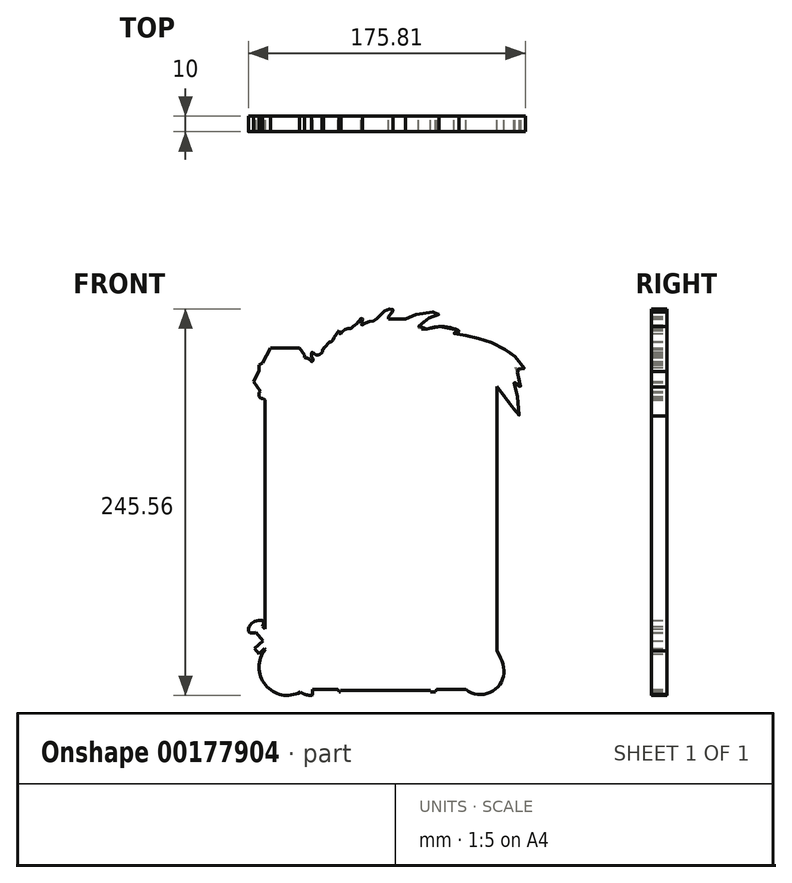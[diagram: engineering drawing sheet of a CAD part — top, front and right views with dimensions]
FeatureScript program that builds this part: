
annotation { "Feature Type Name" : "Feature", "Feature Type Description" : "" }
export const myFeature = defineFeature(function(context is Context, id is Id, definition is map)
    precondition{}
    {
        {
            var Q0;
            Q0=qCreatedBy(makeId("Front.planeOp"),FACE);
            var sketch = newSketch(context, id + "F0", { "sketchPlane" : qUnion([Q0])});
            skLineSegment(sketch, "E0", {"start": v(-74.75, 64.26) * mm, "end": v(-74.75, -81.01) * mm});
            skLineSegment(sketch, "E1", {"start": v(-74.75, -81.01) * mm, "end": v(-76.46, -79.38) * mm});
            skFitSpline(sketch, "E2", {"points": [v(-76.46, -79.38) * mm, v(-75.9, -76.2) * mm, v(-82.58, -77.01) * mm, v(-85.03, -82.89) * mm, v(-80.38, -83.46) * mm], "startDerivative": vector(9.15, 18.87) * mm, "endDerivative": vector(25.07, 3.1) * mm});
            skLineSegment(sketch, "E3", {"start": v(-80.38, -83.46) * mm, "end": v(-76, -88.76) * mm});
            skLineSegment(sketch, "E4", {"start": v(-76, -88.76) * mm, "end": v(-81.56, -93.36) * mm});
            skLineSegment(sketch, "E5", {"start": v(-81.56, -93.36) * mm, "end": v(-78.6, -96.95) * mm});
            skLineSegment(sketch, "E6", {"start": v(-78.6, -96.95) * mm, "end": v(-75.2, -93.38) * mm});
            skLineSegment(sketch, "E7", {"start": v(-75.2, -93.38) * mm, "end": v(-74.52, -94.03) * mm});
            skArc(sketch, "E8", {"start": v(-74.52, -94.03) * mm, "mid": v(-74.52, -116.71) * mm, "end": v(-52.3, -121.24) * mm});
            skLineSegment(sketch, "E9", {"start": v(-44.65, -119.52) * mm, "end": v(-28.42, -119.52) * mm});
            skLineSegment(sketch, "E10", {"start": v(-28.42, -119.52) * mm, "end": v(-28.42, -120.3) * mm});
            skLineSegment(sketch, "E11", {"start": v(-28.42, -120.3) * mm, "end": v(-27.65, -120.3) * mm});
            skLineSegment(sketch, "E12", {"start": v(-27.65, -120.3) * mm, "end": v(-27.65, -121) * mm});
            skLineSegment(sketch, "E13", {"start": v(-27.65, -121) * mm, "end": v(-26.8, -121) * mm});
            skLineSegment(sketch, "E14", {"start": v(-26.8, -121) * mm, "end": v(-26.8, -120.3) * mm});
            skLineSegment(sketch, "E15", {"start": v(-26.8, -120.3) * mm, "end": v(30.46, -120.3) * mm});
            skLineSegment(sketch, "E16", {"start": v(30.46, -120.3) * mm, "end": v(30.46, -121) * mm});
            skLineSegment(sketch, "E17", {"start": v(30.46, -121) * mm, "end": v(33.58, -121) * mm});
            skLineSegment(sketch, "E18", {"start": v(33.58, -121) * mm, "end": v(33.58, -120.3) * mm});
            skLineSegment(sketch, "E19", {"start": v(33.58, -120.3) * mm, "end": v(34.25, -120.3) * mm});
            skLineSegment(sketch, "E20", {"start": v(34.25, -120.3) * mm, "end": v(34.25, -119.52) * mm});
            skLineSegment(sketch, "E21", {"start": v(34.25, -119.52) * mm, "end": v(53.01, -119.52) * mm});
            skFitSpline(sketch, "E22", {"points": [v(53.01, -119.52) * mm, v(67.33, -121.84) * mm, v(76.63, -111.23) * mm, v(72.63, -95.04) * mm], "startDerivative": vector(33.7, -30.73) * mm, "endDerivative": vector(-27.31, 51.01) * mm});
            skLineSegment(sketch, "E23", {"start": v(72.63, -95.04) * mm, "end": v(72.63, 72.94) * mm});
            skFitSpline(sketch, "E24", {"points": [v(72.63, 72.94) * mm, v(85.97, 54.17) * mm, v(85.54, 65.97) * mm, v(83.67, 75.34) * mm, v(87.15, 72.72) * mm, v(86.43, 79.92) * mm, v(84.26, 85.01) * mm, v(90.27, 82.4) * mm, v(86.43, 89.5) * mm, v(80.55, 94.68) * mm, v(70.51, 100.26) * mm, v(61.21, 103.39) * mm, v(52.27, 105.35) * mm, v(45.25, 106.45) * mm, v(48.35, 107.87) * mm, v(37.59, 110.97) * mm, v(27.39, 109.45) * mm, v(22.83, 110.32) * mm, v(27.4, 115.4) * mm, v(34.53, 117.92) * mm, v(35.8, 119.1) * mm, v(33.75, 120.16) * mm, v(19.92, 118.15) * mm, v(14.36, 115.66) * mm], "startDerivative": vector(228.47, -153.01) * mm, "endDerivative": vector(-97.64, -55.3) * mm});
            skLineSegment(sketch, "E25", {"start": v(14.36, 115.66) * mm, "end": v(3.54, 115.66) * mm});
            skLineSegment(sketch, "E26", {"start": v(3.54, 115.66) * mm, "end": v(3.54, 117.49) * mm});
            skFitSpline(sketch, "E27", {"points": [v(3.54, 117.49) * mm, v(6.45, 121.85) * mm, v(1.12, 120.69) * mm, v(-4.7, 115.06) * mm, v(-9.7, 113.76) * mm, v(-13.63, 112.06) * mm, v(-13.7, 113.48) * mm, v(-12.87, 114.86) * mm, v(-13.04, 116.42) * mm, v(-15.65, 113.86) * mm, v(-17.1, 111.96) * mm, v(-18.36, 111.62) * mm, v(-19.71, 110.02) * mm, v(-22.37, 109.76) * mm, v(-25.04, 108.25) * mm, v(-26.48, 106.68) * mm], "startDerivative": vector(53.36, 57.7) * mm, "endDerivative": vector(-20.6, -25.24) * mm});
            skLineSegment(sketch, "E28", {"start": v(-26.48, 106.68) * mm, "end": v(-27.69, 106.68) * mm});
            skLineSegment(sketch, "E29", {"start": v(-27.69, 106.68) * mm, "end": v(-27.69, 108.55) * mm});
            skFitSpline(sketch, "E30", {"points": [v(-27.69, 108.55) * mm, v(-32.67, 101.25) * mm, v(-33.77, 101.3) * mm, v(-36.88, 97.64) * mm, v(-37.62, 97.4) * mm, v(-37.55, 96.34) * mm, v(-38.37, 96.21) * mm, v(-38.29, 95.22) * mm, v(-39.84, 93.4) * mm, v(-42.4, 92.88) * mm, v(-44.86, 94.7) * mm, v(-45.24, 93.92) * mm], "startDerivative": vector(-49.96, -56.7) * mm, "endDerivative": vector(-3.78, -19.88) * mm});
            skLineSegment(sketch, "E31", {"start": v(-45.24, 93.92) * mm, "end": v(-45.24, 91.16) * mm});
            skFitSpline(sketch, "E32", {"points": [v(-45.24, 91.16) * mm, v(-44.38, 90.64) * mm, v(-44.42, 89.26) * mm, v(-45.07, 88.78) * mm, v(-49.64, 91.16) * mm], "startDerivative": vector(5.6, -1.71) * mm, "endDerivative": vector(-22.3, -0.22) * mm});
            skLineSegment(sketch, "E33", {"start": v(-49.64, 91.16) * mm, "end": v(-49.64, 92.95) * mm});
            skLineSegment(sketch, "E34", {"start": v(-49.64, 92.95) * mm, "end": v(-52.8, 97.25) * mm});
            skLineSegment(sketch, "E35", {"start": v(-52.8, 97.25) * mm, "end": v(-71.43, 97.25) * mm});
            skLineSegment(sketch, "E36", {"start": v(-71.43, 97.25) * mm, "end": v(-76.42, 87.83) * mm});
            skLineSegment(sketch, "E37", {"start": v(-76.42, 87.83) * mm, "end": v(-78.54, 86.57) * mm});
            skLineSegment(sketch, "E38", {"start": v(-78.54, 86.57) * mm, "end": v(-78.54, 82.85) * mm});
            skLineSegment(sketch, "E39", {"start": v(-78.54, 82.85) * mm, "end": v(-82.1, 76.14) * mm});
            skLineSegment(sketch, "E40", {"start": v(-82.1, 76.14) * mm, "end": v(-77.68, 69.78) * mm});
            skLineSegment(sketch, "E41", {"start": v(-77.68, 69.78) * mm, "end": v(-78.55, 69.18) * mm});
            skLineSegment(sketch, "E42", {"start": v(-78.55, 69.18) * mm, "end": v(-78.55, 66.48) * mm});
            skLineSegment(sketch, "E43", {"start": v(-78.55, 66.48) * mm, "end": v(-77.4, 65.25) * mm});
            skLineSegment(sketch, "E44", {"start": v(-77.4, 65.25) * mm, "end": v(-76.03, 65.25) * mm});
            skLineSegment(sketch, "E45", {"start": v(-76.03, 65.25) * mm, "end": v(-74.75, 64.26) * mm});
            skFitSpline(sketch, "E46", {"points": [v(-52.3, -121.24) * mm, v(-44.83, -123.37) * mm], "startDerivative": vector(7.01, -5.3) * mm, "endDerivative": vector(7, -0.27) * mm});
            skFitSpline(sketch, "E47", {"points": [v(-44.83, -123.37) * mm, v(-44.65, -119.52) * mm], "startDerivative": vector(1.37, 3.57) * mm, "endDerivative": vector(-0.55, 3.98) * mm});
            skSolve(sketch);
        }
        {
            var Q0;
            Q0 = qSketchRegion(id + "F0", true);
            extrude(context, id + "F1", {"entities" : qUnion([Q0]), "depth" : 10 * mm});
        }
    });
